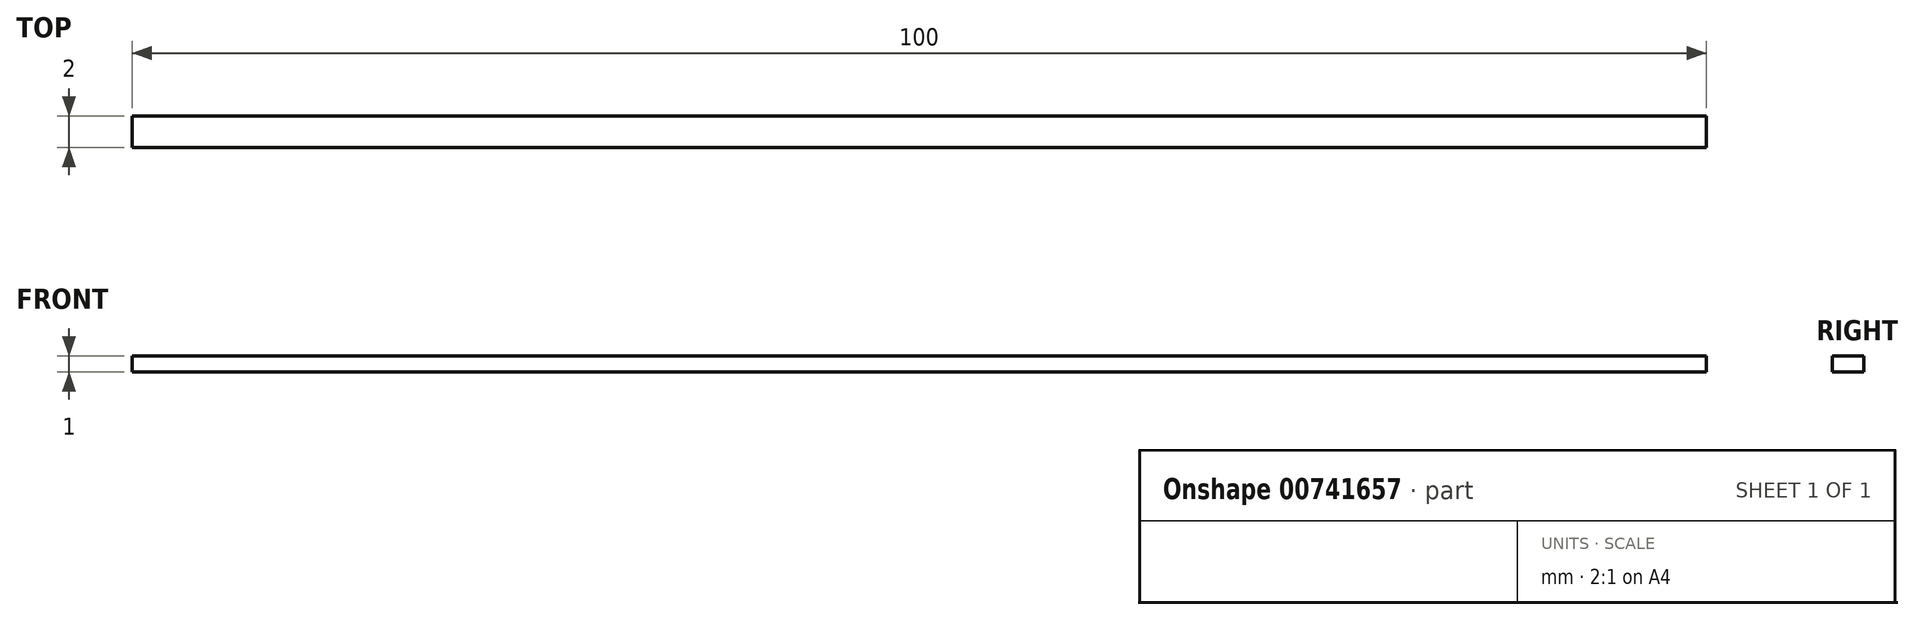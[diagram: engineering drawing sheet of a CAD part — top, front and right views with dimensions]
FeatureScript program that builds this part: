
annotation { "Feature Type Name" : "Feature", "Feature Type Description" : "" }
export const myFeature = defineFeature(function(context is Context, id is Id, definition is map)
    precondition{}
    {
        {
            var Q0;
            Q0=qCreatedBy(makeId("Top.planeOp"),FACE);
            var sketch = newSketch(context, id + "F0", { "sketchPlane" : qUnion([Q0])});
            skLineSegment(sketch, "E0.bottom", {"start": v(50, 1) * mm, "end": v(-50, 1) * mm});
            skLineSegment(sketch, "E0.top", {"start": v(50, -1) * mm, "end": v(-50, -1) * mm});
            skLineSegment(sketch, "E0.left", {"start": v(50, 1) * mm, "end": v(50, -1) * mm});
            skLineSegment(sketch, "E0.right", {"start": v(-50, 1) * mm, "end": v(-50, -1) * mm});
            skPoint(sketch, "E0.middle", {"position": v(0, 0) * mm});
            skSolve(sketch);
        }
        {
            var Q0;
            Q0=makeQuery(id+"F0.imprint","IMPRINT",FACE,{"disambiguationData":[TD([[makeQuery(id+"F0.imprint","IMPRINT",EDGE,{"derivedFrom":sQuery(id+"F0.wireOp",EDGE,"E0.bottom")}),1.0]])]});
            extrude(context, id + "F1", {"entities" : qUnion([Q0]), "depth" : 1 * mm, "offsetDistance" : 25 * mm});
        }
    });
